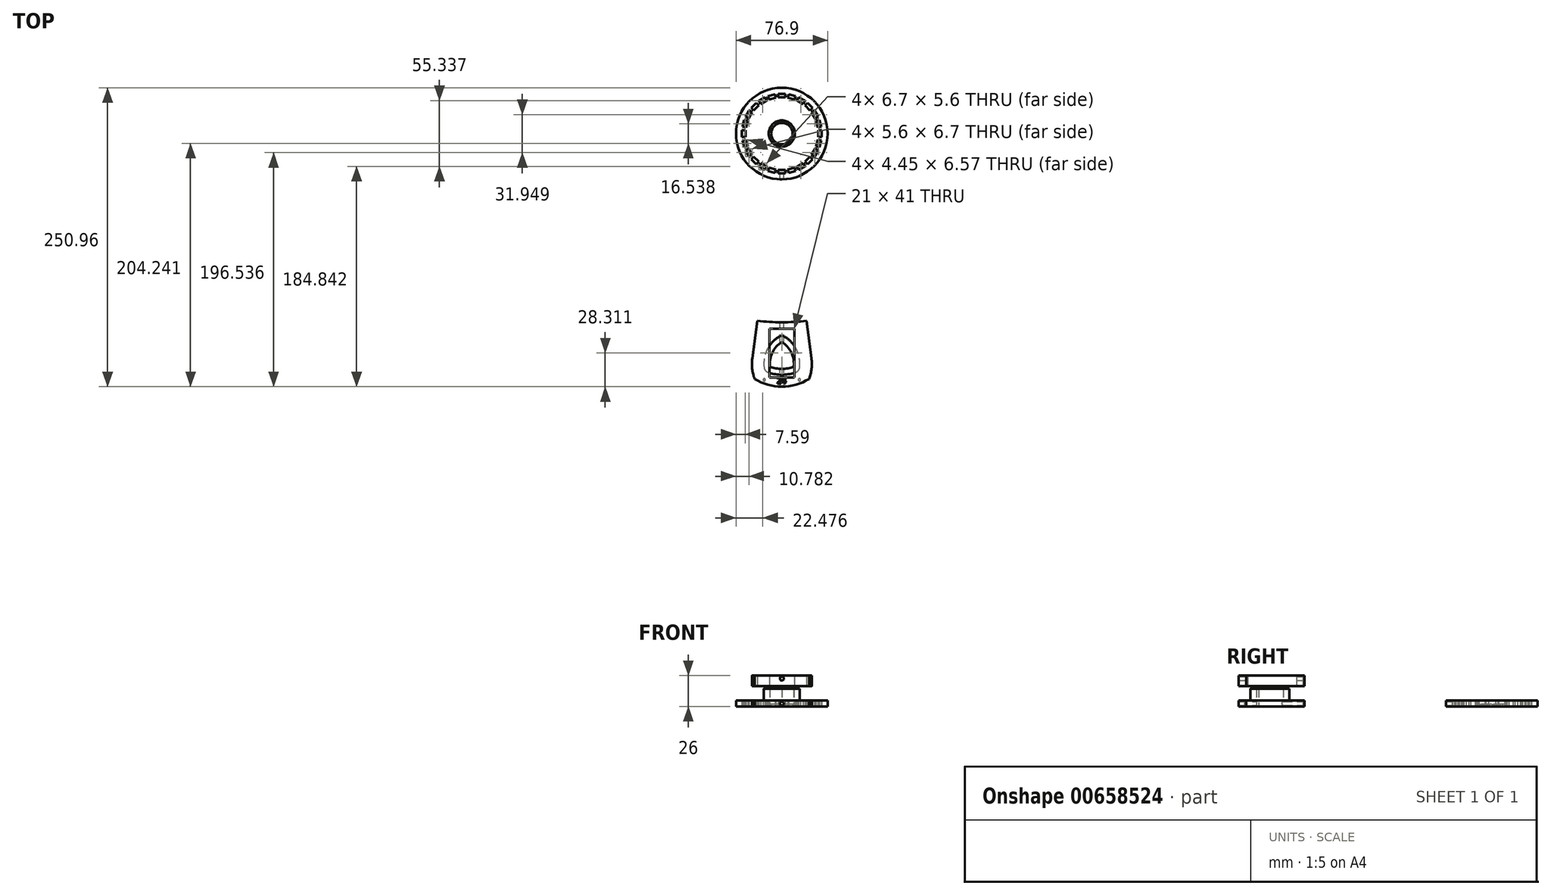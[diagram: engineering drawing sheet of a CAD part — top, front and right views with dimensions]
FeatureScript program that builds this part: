
annotation { "Feature Type Name" : "Feature", "Feature Type Description" : "" }
export const myFeature = defineFeature(function(context is Context, id is Id, definition is map)
    precondition{}
    {
        {
            var Q0;
            Q0=qCreatedBy(makeId("Front.planeOp"),FACE);
            var sketch = newSketch(context, id + "F0", { "sketchPlane" : qUnion([Q0])});
            skLineSegment(sketch, "E0", {"start": v(0, 0) * mm, "end": v(0, 23.65) * mm});
            skSolve(sketch);
        }
        {
            var Q0;
            Q0=qCreatedBy(makeId("Top.planeOp"),FACE);
            var sketch = newSketch(context, id + "F1", { "sketchPlane" : qUnion([Q0])});
            skCircle(sketch, "E1", {"center": v(0, 0) * mm, "radius": 207.24 * mm});
            skArc(sketch, "E2", {"start": v(14.97, -196.23) * mm, "mid": v(12.48, -181.7) * mm, "end": v(2.67, -170.68) * mm});
            skArc(sketch, "E3", {"start": v(-11.77, -200.36) * mm, "mid": v(0, -202.5) * mm, "end": v(11.77, -200.36) * mm});
            skArc(sketch, "E4", {"start": v(-2.67, -170.68) * mm, "mid": v(-12.48, -181.7) * mm, "end": v(-14.97, -196.23) * mm});
            skCircle(sketch, "E5", {"center": v(0, 0) * mm, "radius": 195.94 * mm});
            skArc(sketch, "E6.0", {"start": v(0, -158.43) * mm, "mid": v(-21.5, -177.36) * mm, "end": v(-22.88, -205.97) * mm});
            skArc(sketch, "E6.1", {"start": v(22.88, -205.97) * mm, "mid": v(21.5, -177.36) * mm, "end": v(0, -158.43) * mm});
            skArc(sketch, "E6.2", {"start": v(-22.88, -205.97) * mm, "mid": v(0, -212.5) * mm, "end": v(22.88, -205.97) * mm});
            skCircle(sketch, "E7", {"center": v(0, 0) * mm, "radius": 158.43 * mm});
            skArc(sketch, "E8.filletArc", {"start": v(2.67, -170.68) * mm, "mid": v(0, -169.9) * mm, "end": v(-2.67, -170.68) * mm});
            skPoint(sketch, "E9.visualSharp", {"position": v(-14.47, -199.2) * mm});
            skArc(sketch, "E9.filletArc", {"start": v(-14.97, -196.23) * mm, "mid": v(-13.95, -198.75) * mm, "end": v(-11.77, -200.36) * mm});
            skPoint(sketch, "E10.visualSharp", {"position": v(14.47, -199.2) * mm});
            skArc(sketch, "E10.filletArc", {"start": v(11.77, -200.36) * mm, "mid": v(13.95, -198.75) * mm, "end": v(14.97, -196.23) * mm});
            skLineSegment(sketch, "E11", {"start": v(0, 0) * mm, "end": v(-27.05, -205.47) * mm});
            skLineSegment(sketch, "E12", {"start": v(0, 0) * mm, "end": v(27.05, -205.47) * mm});
            skArc(sketch, "E13.0", {"start": v(0, -174.9) * mm, "mid": v(-7.98, -183.86) * mm, "end": v(-10, -195.68) * mm});
            skArc(sketch, "E13.1", {"start": v(10, -195.68) * mm, "mid": v(7.98, -183.86) * mm, "end": v(0, -174.9) * mm});
            skArc(sketch, "E13.2", {"start": v(-10, -195.68) * mm, "mid": v(0, -197.5) * mm, "end": v(10, -195.68) * mm});
            skPoint(sketch, "E14", {"position": v(-20.68, -157.07) * mm});
            skPoint(sketch, "E15", {"position": v(20.68, -157.07) * mm});
            skCircle(sketch, "E16", {"center": v(-14.75, -206.71) * mm, "radius": 1 * mm});
            skCircle(sketch, "E17", {"center": v(14.75, -206.71) * mm, "radius": 1 * mm});
            skLineSegment(sketch, "E18", {"start": v(-14.47, -199.2) * mm, "end": v(0, -169.2) * mm, "construction": true});
            skLineSegment(sketch, "E19", {"start": v(14.47, -199.2) * mm, "end": v(0, -169.2) * mm, "construction": true});
            skSolve(sketch);
        }
        {
            var Q0;
            {var subQ1=sQuery(id+"F1.wireOp",EDGE,"E6.0");var subQ3=sQuery(id+"F1.wireOp",EDGE,"E11");var subQ4=makeQuery(id+"F1.imprint","INTERSECT",VERTEX,{"derivedFrom":[subQ1,subQ3]});Q0=makeQuery(id+"F1.imprint","IMPRINT",FACE,{"disambiguationData":[TD([[makeQuery(id+"F1.imprint","IMPRINT",EDGE,{"disambiguationData":[TD([[subQ4,1.0]])],"derivedFrom":subQ3}),1.0]])]});}
            var Q1;
            {var subQ1=sQuery(id+"F1.wireOp",EDGE,"E6.1");var subQ3=sQuery(id+"F1.wireOp",EDGE,"E12");var subQ4=makeQuery(id+"F1.imprint","INTERSECT",VERTEX,{"derivedFrom":[subQ1,subQ3]});Q1=makeQuery(id+"F1.imprint","IMPRINT",FACE,{"disambiguationData":[TD([[makeQuery(id+"F1.imprint","IMPRINT",EDGE,{"disambiguationData":[TD([[subQ4,1.0]])],"derivedFrom":subQ3}),-1.0]])]});}
            var Q2;
            {var subQ10=sQuery(id+"F1.wireOp",EDGE,"E2");Q2=makeQuery(id+"F1.imprint","IMPRINT",FACE,{"disambiguationData":[TD([[makeQuery(id+"F1.imprint","IMPRINT",EDGE,{"derivedFrom":subQ10}),-1.0]])]});}
            var Q3;
            {var subQ9=sQuery(id+"F1.wireOp",EDGE,"E3");Q3=makeQuery(id+"F1.imprint","IMPRINT",FACE,{"disambiguationData":[TD([[makeQuery(id+"F1.imprint","IMPRINT",EDGE,{"derivedFrom":subQ9}),-1.0]])]});}
            var Q4;
            {var subQ0=sQuery(id+"F1.wireOp",EDGE,"E6.2");Q4=makeQuery(id+"F1.imprint","IMPRINT",FACE,{"disambiguationData":[TD([[makeQuery(id+"F1.imprint","IMPRINT",EDGE,{"derivedFrom":subQ0}),1.0]])]});}
            extrude(context, id + "F2", {"entities" : qUnion([Q0, Q1, Q2, Q3, Q4]), "depth" : 5 * mm, "offsetDistance" : 25 * mm});
        }
        {
            var Q0;
            {var subQ6=sQuery(id+"F1.wireOp",EDGE,"E2");Q0=makeQuery(id+"F1.imprint","IMPRINT",FACE,{"disambiguationData":[TD([[makeQuery(id+"F1.imprint","IMPRINT",EDGE,{"derivedFrom":subQ6}),1.0]])]});}
            var Q1;
            {var subQ0=sQuery(id+"F1.wireOp",EDGE,"E3");Q1=makeQuery(id+"F1.imprint","IMPRINT",FACE,{"disambiguationData":[TD([[makeQuery(id+"F1.imprint","IMPRINT",EDGE,{"derivedFrom":subQ0}),1.0]])]});}
            extrude(context, id + "F3", {"entities" : qUnion([Q0, Q1]), "operationType" : NewBodyOperationType.ADD, "depth" : 15 * mm, "offsetDistance" : 25 * mm});
        }
        {
            var Q0;
            Q0=makeQuery(id+"F2.opExtrude","SWEPT_EDGE",EDGE,{"disambiguationData":[OSD([sQuery(id+"F1.wireOp",EDGE,"E7"),sQuery(id+"F1.wireOp",EDGE,"E11")])]});
            cPoint(context, id + "F4", {"entities" : qUnion([Q0]), "parameter" : 0.5});
        }
        {
            var Q0;
            Q0=makeQuery(id+"F2.opExtrude","CAP_VERTEX",VERTEX,{"disambiguationData":[OSD([sQuery(id+"F1.wireOp",EDGE,"E7"),sQuery(id+"F1.wireOp",EDGE,"E12")])],"isStart":false});
            var Q1;
            Q1=makeQuery(id+"F2.opExtrude","CAP_VERTEX",VERTEX,{"disambiguationData":[OSD([sQuery(id+"F1.wireOp",EDGE,"E7"),sQuery(id+"F1.wireOp",EDGE,"E11")])],"isStart":false});
            var Q2;
            Q2 = qCreatedBy(id + "F4" ,VERTEX);
            cPlane(context, id + "F5", {"entities" : qUnion([Q0, Q1, Q2]), "cplaneType" : CPlaneType.THREE_POINT, "offset" : 25 * mm, "width" : 150 * mm, "height" : 150 * mm});
        }
        {
            var Q0;
            Q0=makeQuery(id+"F2.opExtrude","CAP_FACE",FACE,{"disambiguationData":[OSD([sQuery(id+"F1.wireOp",EDGE,"E2"),sQuery(id+"F1.wireOp",EDGE,"E3"),sQuery(id+"F1.wireOp",EDGE,"E4"),sQuery(id+"F1.wireOp",EDGE,"E6.0"),sQuery(id+"F1.wireOp",EDGE,"E6.1"),sQuery(id+"F1.wireOp",EDGE,"E6.2"),sQuery(id+"F1.wireOp",EDGE,"E7"),sQuery(id+"F1.wireOp",EDGE,"E8.filletArc"),sQuery(id+"F1.wireOp",EDGE,"E9.filletArc"),sQuery(id+"F1.wireOp",EDGE,"E10.filletArc"),sQuery(id+"F1.wireOp",EDGE,"E11"),sQuery(id+"F1.wireOp",EDGE,"E12"),sQuery(id+"F1.wireOp",EDGE,"E16"),sQuery(id+"F1.wireOp",EDGE,"E17")])],"isStart":false});
            var sketch = newSketch(context, id + "F6", { "sketchPlane" : qUnion([Q0])});
            skText(sketch, "E20", { "text": "24\n", "fontName": "OpenSans-Regular.ttf"});
            skPoint(sketch, "E21", {"position": v(0, -207.24) * mm});
            const initialGuessF6  = {"E20": [-0.00413, -0.20974, 1, 0, 0.005]};
            skSetInitialGuess(sketch, initialGuessF6);
            skSolve(sketch);
        }
        {
            var Q0;
            Q0 = qSketchRegion(id + "F6", true);
            extrude(context, id + "F7", {"entities" : qUnion([Q0]), "operationType" : NewBodyOperationType.REMOVE, "depth" : -0.4 * mm, "offsetDistance" : 25 * mm});
        }
        {
            var Q0;
            Q0=qCreatedBy(id+"F5.planeOp",FACE);
            var sketch = newSketch(context, id + "F8", { "sketchPlane" : qUnion([Q0])});
            skPoint(sketch, "E22.0", {"position": v(-20.68, 5) * mm});
            skPoint(sketch, "E23.0", {"position": v(20.68, 5) * mm});
            skPoint(sketch, "E24", {"position": v(0, 2.5) * mm});
            skPoint(sketch, "E25.0", {"position": v(20.68, 0) * mm});
            skPoint(sketch, "E26.0", {"position": v(-20.68, 0) * mm});
            skSolve(sketch);
        }
        {
            var Q0;
            Q0=sQuery(id+"F8.wireOp",VERTEX,"E24");
            var Q1;
            Q1=makeQuery(id+"F2.opExtrude","SWEPT_BODY",BODY,{"disambiguationData":[OSD([sQuery(id+"F1.wireOp",EDGE,"E2"),sQuery(id+"F1.wireOp",EDGE,"E3"),sQuery(id+"F1.wireOp",EDGE,"E4"),sQuery(id+"F1.wireOp",EDGE,"E6.0"),sQuery(id+"F1.wireOp",EDGE,"E6.1"),sQuery(id+"F1.wireOp",EDGE,"E6.2"),sQuery(id+"F1.wireOp",EDGE,"E7"),sQuery(id+"F1.wireOp",EDGE,"E8.filletArc"),sQuery(id+"F1.wireOp",EDGE,"E9.filletArc"),sQuery(id+"F1.wireOp",EDGE,"E10.filletArc"),sQuery(id+"F1.wireOp",EDGE,"E11"),sQuery(id+"F1.wireOp",EDGE,"E12")])]});
            hole(context, id + "F9", {"style" : HoleStyle.SIMPLE, "endStyle" : HoleEndStyle.THROUGH, "standardTappedOrClearance" : lookupTablePath({ "fit" : "Normal", "standard" : "ISO", "size" : "M3", "type" : "Clearance" }), "standardBlindInLast" : lookupTablePath({ "fit" : "Standard", "standard" : "ISO", "size" : "M3", "type" : "Clearance" }), "holeDiameter" : 3.3 * mm, "majorDiameter" : 5 * mm, "isTappedThrough" : true, "tappedDepth" : 12 * mm, "tapClearance" : 3, "startFromSketch" : true, "locations" : qUnion([Q0]), "scope" : qUnion([Q1])});
        }
        {
            var Q0;
            Q0=qCreatedBy(makeId("Top.planeOp"),FACE);
            var sketch = newSketch(context, id + "F10", { "sketchPlane" : qUnion([Q0])});
            skCircle(sketch, "E27", {"center": v(0, 0) * mm, "radius": 38.45 * mm});
            skLineSegment(sketch, "E28.bottom", {"start": v(-3, -30.45) * mm, "end": v(3, -30.45) * mm});
            skLineSegment(sketch, "E28.top", {"start": v(-3, -33.45) * mm, "end": v(3, -33.45) * mm});
            skLineSegment(sketch, "E28.left", {"start": v(-3, -30.45) * mm, "end": v(-3, -33.45) * mm});
            skLineSegment(sketch, "E28.right", {"start": v(3, -30.45) * mm, "end": v(3, -33.45) * mm});
            skCircle(sketch, "E29", {"center": v(0, 0) * mm, "radius": 11 * mm});
            skLineSegment(sketch, "E30.1.0", {"start": v(-10.78, -28.63) * mm, "end": v(-4.98, -30.19) * mm});
            skLineSegment(sketch, "E30.1.1", {"start": v(-4.98, -30.19) * mm, "end": v(-5.76, -33.09) * mm});
            skLineSegment(sketch, "E30.1.2", {"start": v(-11.55, -31.53) * mm, "end": v(-5.76, -33.09) * mm});
            skLineSegment(sketch, "E30.1.3", {"start": v(-10.78, -28.63) * mm, "end": v(-11.55, -31.53) * mm});
            skLineSegment(sketch, "E30.2.0", {"start": v(-17.82, -24.87) * mm, "end": v(-12.63, -27.87) * mm});
            skLineSegment(sketch, "E30.2.1", {"start": v(-12.63, -27.87) * mm, "end": v(-14.13, -30.47) * mm});
            skLineSegment(sketch, "E30.2.2", {"start": v(-19.32, -27.47) * mm, "end": v(-14.13, -30.47) * mm});
            skLineSegment(sketch, "E30.2.3", {"start": v(-17.82, -24.87) * mm, "end": v(-19.32, -27.47) * mm});
            skLineSegment(sketch, "E30.3.0", {"start": v(-23.65, -19.4) * mm, "end": v(-19.4, -23.65) * mm});
            skLineSegment(sketch, "E30.3.1", {"start": v(-19.4, -23.65) * mm, "end": v(-21.53, -25.77) * mm});
            skLineSegment(sketch, "E30.3.2", {"start": v(-25.77, -21.53) * mm, "end": v(-21.53, -25.77) * mm});
            skLineSegment(sketch, "E30.3.3", {"start": v(-23.65, -19.4) * mm, "end": v(-25.77, -21.53) * mm});
            skLineSegment(sketch, "E30.4.0", {"start": v(-27.87, -12.63) * mm, "end": v(-24.87, -17.82) * mm});
            skLineSegment(sketch, "E30.4.1", {"start": v(-24.87, -17.82) * mm, "end": v(-27.47, -19.32) * mm});
            skLineSegment(sketch, "E30.4.2", {"start": v(-30.47, -14.13) * mm, "end": v(-27.47, -19.32) * mm});
            skLineSegment(sketch, "E30.4.3", {"start": v(-27.87, -12.63) * mm, "end": v(-30.47, -14.13) * mm});
            skLineSegment(sketch, "E30.5.0", {"start": v(-30.19, -4.98) * mm, "end": v(-28.63, -10.78) * mm});
            skLineSegment(sketch, "E30.5.1", {"start": v(-28.63, -10.78) * mm, "end": v(-31.53, -11.55) * mm});
            skLineSegment(sketch, "E30.5.2", {"start": v(-33.09, -5.76) * mm, "end": v(-31.53, -11.55) * mm});
            skLineSegment(sketch, "E30.5.3", {"start": v(-30.19, -4.98) * mm, "end": v(-33.09, -5.76) * mm});
            skLineSegment(sketch, "E30.6.0", {"start": v(-30.45, 3) * mm, "end": v(-30.45, -3) * mm});
            skLineSegment(sketch, "E30.6.1", {"start": v(-30.45, -3) * mm, "end": v(-33.45, -3) * mm});
            skLineSegment(sketch, "E30.6.2", {"start": v(-33.45, 3) * mm, "end": v(-33.45, -3) * mm});
            skLineSegment(sketch, "E30.6.3", {"start": v(-30.45, 3) * mm, "end": v(-33.45, 3) * mm});
            skLineSegment(sketch, "E30.7.0", {"start": v(-28.63, 10.78) * mm, "end": v(-30.19, 4.98) * mm});
            skLineSegment(sketch, "E30.7.1", {"start": v(-30.19, 4.98) * mm, "end": v(-33.09, 5.76) * mm});
            skLineSegment(sketch, "E30.7.2", {"start": v(-31.53, 11.55) * mm, "end": v(-33.09, 5.76) * mm});
            skLineSegment(sketch, "E30.7.3", {"start": v(-28.63, 10.78) * mm, "end": v(-31.53, 11.55) * mm});
            skLineSegment(sketch, "E30.8.0", {"start": v(-24.87, 17.82) * mm, "end": v(-27.87, 12.63) * mm});
            skLineSegment(sketch, "E30.8.1", {"start": v(-27.87, 12.63) * mm, "end": v(-30.47, 14.13) * mm});
            skLineSegment(sketch, "E30.8.2", {"start": v(-27.47, 19.32) * mm, "end": v(-30.47, 14.13) * mm});
            skLineSegment(sketch, "E30.8.3", {"start": v(-24.87, 17.82) * mm, "end": v(-27.47, 19.32) * mm});
            skLineSegment(sketch, "E30.9.0", {"start": v(-19.4, 23.65) * mm, "end": v(-23.65, 19.4) * mm});
            skLineSegment(sketch, "E30.9.1", {"start": v(-23.65, 19.4) * mm, "end": v(-25.77, 21.53) * mm});
            skLineSegment(sketch, "E30.9.2", {"start": v(-21.53, 25.77) * mm, "end": v(-25.77, 21.53) * mm});
            skLineSegment(sketch, "E30.9.3", {"start": v(-19.4, 23.65) * mm, "end": v(-21.53, 25.77) * mm});
            skLineSegment(sketch, "E30.10.0", {"start": v(-12.63, 27.87) * mm, "end": v(-17.82, 24.87) * mm});
            skLineSegment(sketch, "E30.10.1", {"start": v(-17.82, 24.87) * mm, "end": v(-19.32, 27.47) * mm});
            skLineSegment(sketch, "E30.10.2", {"start": v(-14.13, 30.47) * mm, "end": v(-19.32, 27.47) * mm});
            skLineSegment(sketch, "E30.10.3", {"start": v(-12.63, 27.87) * mm, "end": v(-14.13, 30.47) * mm});
            skLineSegment(sketch, "E30.11.0", {"start": v(-4.98, 30.19) * mm, "end": v(-10.78, 28.63) * mm});
            skLineSegment(sketch, "E30.11.1", {"start": v(-10.78, 28.63) * mm, "end": v(-11.55, 31.53) * mm});
            skLineSegment(sketch, "E30.11.2", {"start": v(-5.76, 33.09) * mm, "end": v(-11.55, 31.53) * mm});
            skLineSegment(sketch, "E30.11.3", {"start": v(-4.98, 30.19) * mm, "end": v(-5.76, 33.09) * mm});
            skLineSegment(sketch, "E30.anchor1", {"start": v(0, 0) * mm, "end": v(-3, -30.45) * mm, "construction": true});
            skLineSegment(sketch, "E30.anchor2", {"start": v(0, 0) * mm, "end": v(4.98, -30.19) * mm, "construction": true});
            skCircle(sketch, "E31", {"center": v(0, 0) * mm, "radius": 9 * mm});
            skLineSegment(sketch, "E32.1.12.0", {"start": v(3, 30.45) * mm, "end": v(-3, 30.45) * mm});
            skLineSegment(sketch, "E32.3.12.0", {"start": v(-3, 30.45) * mm, "end": v(-3, 33.45) * mm});
            skLineSegment(sketch, "E32.6.12.0", {"start": v(3, 33.45) * mm, "end": v(-3, 33.45) * mm});
            skLineSegment(sketch, "E32.9.12.0", {"start": v(3, 30.45) * mm, "end": v(3, 33.45) * mm});
            skLineSegment(sketch, "E32.1.13.0", {"start": v(10.78, 28.63) * mm, "end": v(4.98, 30.19) * mm});
            skLineSegment(sketch, "E32.3.13.0", {"start": v(4.98, 30.19) * mm, "end": v(5.76, 33.09) * mm});
            skLineSegment(sketch, "E32.6.13.0", {"start": v(11.55, 31.53) * mm, "end": v(5.76, 33.09) * mm});
            skLineSegment(sketch, "E32.9.13.0", {"start": v(10.78, 28.63) * mm, "end": v(11.55, 31.53) * mm});
            skLineSegment(sketch, "E32.1.14.0", {"start": v(17.82, 24.87) * mm, "end": v(12.63, 27.87) * mm});
            skLineSegment(sketch, "E32.3.14.0", {"start": v(12.63, 27.87) * mm, "end": v(14.13, 30.47) * mm});
            skLineSegment(sketch, "E32.6.14.0", {"start": v(19.32, 27.47) * mm, "end": v(14.13, 30.47) * mm});
            skLineSegment(sketch, "E32.9.14.0", {"start": v(17.82, 24.87) * mm, "end": v(19.32, 27.47) * mm});
            skLineSegment(sketch, "E32.1.15.0", {"start": v(23.65, 19.4) * mm, "end": v(19.4, 23.65) * mm});
            skLineSegment(sketch, "E32.3.15.0", {"start": v(19.4, 23.65) * mm, "end": v(21.53, 25.77) * mm});
            skLineSegment(sketch, "E32.6.15.0", {"start": v(25.77, 21.53) * mm, "end": v(21.53, 25.77) * mm});
            skLineSegment(sketch, "E32.9.15.0", {"start": v(23.65, 19.4) * mm, "end": v(25.77, 21.53) * mm});
            skLineSegment(sketch, "E32.1.16.0", {"start": v(27.87, 12.63) * mm, "end": v(24.87, 17.82) * mm});
            skLineSegment(sketch, "E32.3.16.0", {"start": v(24.87, 17.82) * mm, "end": v(27.47, 19.32) * mm});
            skLineSegment(sketch, "E32.6.16.0", {"start": v(30.47, 14.13) * mm, "end": v(27.47, 19.32) * mm});
            skLineSegment(sketch, "E32.9.16.0", {"start": v(27.87, 12.63) * mm, "end": v(30.47, 14.13) * mm});
            skLineSegment(sketch, "E32.1.17.0", {"start": v(30.19, 4.98) * mm, "end": v(28.63, 10.78) * mm});
            skLineSegment(sketch, "E32.3.17.0", {"start": v(28.63, 10.78) * mm, "end": v(31.53, 11.55) * mm});
            skLineSegment(sketch, "E32.6.17.0", {"start": v(33.09, 5.76) * mm, "end": v(31.53, 11.55) * mm});
            skLineSegment(sketch, "E32.9.17.0", {"start": v(30.19, 4.98) * mm, "end": v(33.09, 5.76) * mm});
            skLineSegment(sketch, "E32.1.18.0", {"start": v(30.45, -3) * mm, "end": v(30.45, 3) * mm});
            skLineSegment(sketch, "E32.3.18.0", {"start": v(30.45, 3) * mm, "end": v(33.45, 3) * mm});
            skLineSegment(sketch, "E32.6.18.0", {"start": v(33.45, -3) * mm, "end": v(33.45, 3) * mm});
            skLineSegment(sketch, "E32.9.18.0", {"start": v(30.45, -3) * mm, "end": v(33.45, -3) * mm});
            skLineSegment(sketch, "E32.1.19.0", {"start": v(28.63, -10.78) * mm, "end": v(30.19, -4.98) * mm});
            skLineSegment(sketch, "E32.3.19.0", {"start": v(30.19, -4.98) * mm, "end": v(33.09, -5.76) * mm});
            skLineSegment(sketch, "E32.6.19.0", {"start": v(31.53, -11.55) * mm, "end": v(33.09, -5.76) * mm});
            skLineSegment(sketch, "E32.9.19.0", {"start": v(28.63, -10.78) * mm, "end": v(31.53, -11.55) * mm});
            skLineSegment(sketch, "E32.1.20.0", {"start": v(24.87, -17.82) * mm, "end": v(27.87, -12.63) * mm});
            skLineSegment(sketch, "E32.3.20.0", {"start": v(27.87, -12.63) * mm, "end": v(30.47, -14.13) * mm});
            skLineSegment(sketch, "E32.6.20.0", {"start": v(27.47, -19.32) * mm, "end": v(30.47, -14.13) * mm});
            skLineSegment(sketch, "E32.9.20.0", {"start": v(24.87, -17.82) * mm, "end": v(27.47, -19.32) * mm});
            skLineSegment(sketch, "E32.1.21.0", {"start": v(19.4, -23.65) * mm, "end": v(23.65, -19.4) * mm});
            skLineSegment(sketch, "E32.3.21.0", {"start": v(23.65, -19.4) * mm, "end": v(25.77, -21.53) * mm});
            skLineSegment(sketch, "E32.6.21.0", {"start": v(21.53, -25.77) * mm, "end": v(25.77, -21.53) * mm});
            skLineSegment(sketch, "E32.9.21.0", {"start": v(19.4, -23.65) * mm, "end": v(21.53, -25.77) * mm});
            skLineSegment(sketch, "E32.1.22.0", {"start": v(12.63, -27.87) * mm, "end": v(17.82, -24.87) * mm});
            skLineSegment(sketch, "E32.3.22.0", {"start": v(17.82, -24.87) * mm, "end": v(19.32, -27.47) * mm});
            skLineSegment(sketch, "E32.6.22.0", {"start": v(14.13, -30.47) * mm, "end": v(19.32, -27.47) * mm});
            skLineSegment(sketch, "E32.9.22.0", {"start": v(12.63, -27.87) * mm, "end": v(14.13, -30.47) * mm});
            skLineSegment(sketch, "E32.1.23.0", {"start": v(4.98, -30.19) * mm, "end": v(10.78, -28.63) * mm});
            skLineSegment(sketch, "E32.3.23.0", {"start": v(10.78, -28.63) * mm, "end": v(11.55, -31.53) * mm});
            skLineSegment(sketch, "E32.6.23.0", {"start": v(5.76, -33.09) * mm, "end": v(11.55, -31.53) * mm});
            skLineSegment(sketch, "E32.9.23.0", {"start": v(4.98, -30.19) * mm, "end": v(5.76, -33.09) * mm});
            skSolve(sketch);
        }
        {
            var Q0;
            Q0=makeQuery(id+"F10.imprint","IMPRINT",FACE,{"disambiguationData":[TD([[makeQuery(id+"F10.imprint","IMPRINT",EDGE,{"derivedFrom":sQuery(id+"F10.wireOp",EDGE,"E27")}),1.0]])]});
            extrude(context, id + "F11", {"entities" : qUnion([Q0]), "depth" : 5 * mm, "offsetDistance" : 25 * mm});
        }
        {
            var Q0;
            Q0=makeQuery(id+"F10.imprint","IMPRINT",FACE,{"disambiguationData":[TD([[makeQuery(id+"F10.imprint","IMPRINT",EDGE,{"derivedFrom":sQuery(id+"F10.wireOp",EDGE,"E29")}),1.0]])]});
            extrude(context, id + "F12", {"entities" : qUnion([Q0]), "operationType" : NewBodyOperationType.ADD, "depth" : 2 * mm, "offsetDistance" : 25 * mm});
        }
        {
            var Q0;
            Q0=makeQuery(id+"F11.opExtrude","SWEPT_FACE",FACE,{"disambiguationData":[OSD([sQuery(id+"F10.wireOp",EDGE,"E28.top")])]});
            var sketch = newSketch(context, id + "F13", { "sketchPlane" : qUnion([Q0])});
            skLineSegment(sketch, "E33.0.0", {"start": v(-3, 0) * mm, "end": v(3, 0) * mm});
            skLineSegment(sketch, "E33.0.1", {"start": v(3, 0) * mm, "end": v(3, 5) * mm});
            skLineSegment(sketch, "E33.0.2", {"start": v(3, 5) * mm, "end": v(-3, 5) * mm});
            skLineSegment(sketch, "E33.0.3", {"start": v(-3, 5) * mm, "end": v(-3, 0) * mm});
            skPoint(sketch, "E34.0", {"position": v(0, 2.5) * mm});
            skSolve(sketch);
        }
        {
            var Q0;
            Q0=sQuery(id+"F13.wireOp",VERTEX,"E34.0");
            var Q1;
            Q1=makeQuery(id+"F11.opExtrude","SWEPT_BODY",BODY,{"disambiguationData":[OSD([sQuery(id+"F10.wireOp",EDGE,"E27"),sQuery(id+"F10.wireOp",EDGE,"E28.bottom"),sQuery(id+"F10.wireOp",EDGE,"E28.top"),sQuery(id+"F10.wireOp",EDGE,"E28.left"),sQuery(id+"F10.wireOp",EDGE,"E28.right"),sQuery(id+"F10.wireOp",EDGE,"E29"),sQuery(id+"F10.wireOp",EDGE,"E30.1.0"),sQuery(id+"F10.wireOp",EDGE,"E30.1.1"),sQuery(id+"F10.wireOp",EDGE,"E30.1.2"),sQuery(id+"F10.wireOp",EDGE,"E30.1.3"),sQuery(id+"F10.wireOp",EDGE,"E30.2.0"),sQuery(id+"F10.wireOp",EDGE,"E30.2.1"),sQuery(id+"F10.wireOp",EDGE,"E30.2.2"),sQuery(id+"F10.wireOp",EDGE,"E30.2.3"),sQuery(id+"F10.wireOp",EDGE,"E30.3.0"),sQuery(id+"F10.wireOp",EDGE,"E30.3.1"),sQuery(id+"F10.wireOp",EDGE,"E30.3.2"),sQuery(id+"F10.wireOp",EDGE,"E30.3.3"),sQuery(id+"F10.wireOp",EDGE,"E30.4.0"),sQuery(id+"F10.wireOp",EDGE,"E30.4.1"),sQuery(id+"F10.wireOp",EDGE,"E30.4.2"),sQuery(id+"F10.wireOp",EDGE,"E30.4.3"),sQuery(id+"F10.wireOp",EDGE,"E30.5.0"),sQuery(id+"F10.wireOp",EDGE,"E30.5.1"),sQuery(id+"F10.wireOp",EDGE,"E30.5.2"),sQuery(id+"F10.wireOp",EDGE,"E30.5.3"),sQuery(id+"F10.wireOp",EDGE,"E30.6.0"),sQuery(id+"F10.wireOp",EDGE,"E30.6.1"),sQuery(id+"F10.wireOp",EDGE,"E30.6.2"),sQuery(id+"F10.wireOp",EDGE,"E30.6.3"),sQuery(id+"F10.wireOp",EDGE,"E30.7.0"),sQuery(id+"F10.wireOp",EDGE,"E30.7.1"),sQuery(id+"F10.wireOp",EDGE,"E30.7.2"),sQuery(id+"F10.wireOp",EDGE,"E30.7.3"),sQuery(id+"F10.wireOp",EDGE,"E30.8.0"),sQuery(id+"F10.wireOp",EDGE,"E30.8.1"),sQuery(id+"F10.wireOp",EDGE,"E30.8.2"),sQuery(id+"F10.wireOp",EDGE,"E30.8.3"),sQuery(id+"F10.wireOp",EDGE,"E30.9.0"),sQuery(id+"F10.wireOp",EDGE,"E30.9.1"),sQuery(id+"F10.wireOp",EDGE,"E30.9.2"),sQuery(id+"F10.wireOp",EDGE,"E30.9.3"),sQuery(id+"F10.wireOp",EDGE,"E30.10.0"),sQuery(id+"F10.wireOp",EDGE,"E30.10.1"),sQuery(id+"F10.wireOp",EDGE,"E30.10.2"),sQuery(id+"F10.wireOp",EDGE,"E30.10.3"),sQuery(id+"F10.wireOp",EDGE,"E30.11.0"),sQuery(id+"F10.wireOp",EDGE,"E30.11.1"),sQuery(id+"F10.wireOp",EDGE,"E30.11.2"),sQuery(id+"F10.wireOp",EDGE,"E30.11.3"),sQuery(id+"F10.wireOp",EDGE,"E30.12.0"),sQuery(id+"F10.wireOp",EDGE,"E30.12.1"),sQuery(id+"F10.wireOp",EDGE,"E30.12.2"),sQuery(id+"F10.wireOp",EDGE,"E30.12.3"),sQuery(id+"F10.wireOp",EDGE,"E30.13.0"),sQuery(id+"F10.wireOp",EDGE,"E30.13.1"),sQuery(id+"F10.wireOp",EDGE,"E30.13.2"),sQuery(id+"F10.wireOp",EDGE,"E30.13.3"),sQuery(id+"F10.wireOp",EDGE,"E30.14.0"),sQuery(id+"F10.wireOp",EDGE,"E30.14.1"),sQuery(id+"F10.wireOp",EDGE,"E30.14.2"),sQuery(id+"F10.wireOp",EDGE,"E30.14.3")])]});
            hole(context, id + "F14", {"style" : HoleStyle.SIMPLE, "endStyle" : HoleEndStyle.THROUGH, "standardTappedOrClearance" : lookupTablePath({ "fit" : "Normal", "standard" : "ISO", "size" : "M3", "type" : "Clearance" }), "standardBlindInLast" : lookupTablePath({ "fit" : "Standard", "standard" : "ISO", "size" : "M3", "type" : "Clearance" }), "holeDiameter" : 3.3 * mm, "majorDiameter" : 5 * mm, "isTappedThrough" : true, "tappedDepth" : 12 * mm, "tapClearance" : 3, "startFromSketch" : true, "locations" : qUnion([Q0]), "scope" : qUnion([Q1])});
        }
        {
            var Q0;
            Q0=makeQuery(id+"F3.opExtrude","CAP_FACE",FACE,{"disambiguationData":[OSD([sQuery(id+"F1.wireOp",EDGE,"E2"),sQuery(id+"F1.wireOp",EDGE,"E3"),sQuery(id+"F1.wireOp",EDGE,"E4"),sQuery(id+"F1.wireOp",EDGE,"E8.filletArc"),sQuery(id+"F1.wireOp",EDGE,"E9.filletArc"),sQuery(id+"F1.wireOp",EDGE,"E10.filletArc"),sQuery(id+"F1.wireOp",EDGE,"E13.0"),sQuery(id+"F1.wireOp",EDGE,"E13.1"),sQuery(id+"F1.wireOp",EDGE,"E13.2")])],"isStart":false});
            cPlane(context, id + "F15", {"entities" : qUnion([Q0]), "cplaneType" : CPlaneType.OFFSET, "offset" : 2 * mm, "width" : 150 * mm, "height" : 150 * mm});
        }
        {
            var Q0;
            Q0=qCreatedBy(id+"F15.planeOp",FACE);
            var sketch = newSketch(context, id + "F16", { "sketchPlane" : qUnion([Q0])});
            skLineSegment(sketch, "E35.bottom", {"start": v(-10, -164.2) * mm, "end": v(10, -164.2) * mm, "construction": true});
            skLineSegment(sketch, "E35.top", {"start": v(-10, -204.2) * mm, "end": v(10, -204.2) * mm, "construction": true});
            skLineSegment(sketch, "E35.left", {"start": v(-10, -164.2) * mm, "end": v(-10, -204.2) * mm, "construction": true});
            skLineSegment(sketch, "E35.right", {"start": v(10, -164.2) * mm, "end": v(10, -204.2) * mm, "construction": true});
            skLineSegment(sketch, "E36.0", {"start": v(0, 0) * mm, "end": v(-27.05, -205.47) * mm});
            skCircle(sketch, "E37.0", {"center": v(0, 0) * mm, "radius": 158.43 * mm});
            skLineSegment(sketch, "E38.0", {"start": v(0, 0) * mm, "end": v(27.05, -205.47) * mm});
            skArc(sketch, "E39.0", {"start": v(0, -158.43) * mm, "mid": v(-21.5, -177.36) * mm, "end": v(-22.88, -205.97) * mm});
            skArc(sketch, "E40.0", {"start": v(22.88, -205.97) * mm, "mid": v(21.5, -177.36) * mm, "end": v(0, -158.43) * mm});
            skArc(sketch, "E41.0", {"start": v(-22.88, -205.97) * mm, "mid": v(0, -212.5) * mm, "end": v(22.88, -205.97) * mm});
            skLineSegment(sketch, "E42", {"start": v(0, -169.2) * mm, "end": v(0, -176.7) * mm, "construction": true});
            skLineSegment(sketch, "E43", {"start": v(0, -176.7) * mm, "end": v(0, -184.2) * mm, "construction": true});
            skPoint(sketch, "E44.0", {"position": v(-14.47, -199.2) * mm});
            skPoint(sketch, "E45.0", {"position": v(14.47, -199.2) * mm});
            skLineSegment(sketch, "E46", {"start": v(-14.47, -199.2) * mm, "end": v(0, -199.2) * mm, "construction": true});
            skLineSegment(sketch, "E47", {"start": v(0, -199.2) * mm, "end": v(14.47, -199.2) * mm, "construction": true});
            skLineSegment(sketch, "E48", {"start": v(0, -184.2) * mm, "end": v(0, -191.7) * mm, "construction": true});
            skLineSegment(sketch, "E49", {"start": v(0, -191.7) * mm, "end": v(0, -199.2) * mm, "construction": true});
            skLineSegment(sketch, "E50.0", {"start": v(-10.5, -163.7) * mm, "end": v(10.5, -163.7) * mm});
            skLineSegment(sketch, "E50.1", {"start": v(-10.5, -163.7) * mm, "end": v(-10.5, -204.7) * mm});
            skLineSegment(sketch, "E50.2", {"start": v(-10.5, -204.7) * mm, "end": v(10.5, -204.7) * mm});
            skLineSegment(sketch, "E50.3", {"start": v(10.5, -163.7) * mm, "end": v(10.5, -204.7) * mm});
            skSolve(sketch);
        }
        {
            var Q0;
            {var subQ0=sQuery(id+"F16.wireOp",EDGE,"E39.0");var subQ1=sQuery(id+"F16.wireOp",EDGE,"E36.0");var subQ2=makeQuery(id+"F16.imprint","INTERSECT",VERTEX,{"derivedFrom":[subQ1,subQ0]});Q0=makeQuery(id+"F16.imprint","IMPRINT",FACE,{"disambiguationData":[TD([[makeQuery(id+"F16.imprint","IMPRINT",EDGE,{"disambiguationData":[TD([[subQ2,1.0]])],"derivedFrom":subQ1}),1.0]])]});}
            var Q1;
            {var subQ0=sQuery(id+"F16.wireOp",EDGE,"E40.0");var subQ5=sQuery(id+"F16.wireOp",EDGE,"E38.0");var subQ7=makeQuery(id+"F16.imprint","INTERSECT",VERTEX,{"derivedFrom":[subQ5,subQ0]});Q1=makeQuery(id+"F16.imprint","IMPRINT",FACE,{"disambiguationData":[TD([[makeQuery(id+"F16.imprint","IMPRINT",EDGE,{"disambiguationData":[TD([[subQ7,1.0]])],"derivedFrom":subQ5}),-1.0]])]});}
            var Q2;
            {var subQ5=sQuery(id+"F16.wireOp",EDGE,"E41.0");Q2=makeQuery(id+"F16.imprint","IMPRINT",FACE,{"disambiguationData":[TD([[makeQuery(id+"F16.imprint","IMPRINT",EDGE,{"derivedFrom":subQ5}),1.0]])]});}
            var Q3;
            {var subQ1=sQuery(id+"F16.wireOp",EDGE,"E39.0");var subQ3=sQuery(id+"F16.wireOp",EDGE,"E50.0");var subQ4=makeQuery(id+"F16.imprint","INTERSECT",VERTEX,{"derivedFrom":[subQ1,subQ3]});Q3=makeQuery(id+"F16.imprint","IMPRINT",FACE,{"disambiguationData":[TD([[makeQuery(id+"F16.imprint","IMPRINT",EDGE,{"disambiguationData":[TD([[subQ4,-1.0]])],"derivedFrom":subQ3}),1.0]])]});}
            extrude(context, id + "F17", {"entities" : qUnion([Q0, Q1, Q2, Q3]), "depth" : 9 * mm, "offsetDistance" : 25 * mm});
        }
        {
            var Q0;
            Q0=makeQuery(id+"F17.opExtrude","CAP_VERTEX",VERTEX,{"disambiguationData":[OSD([sQuery(id+"F16.wireOp",EDGE,"E37.0"),sQuery(id+"F16.wireOp",EDGE,"E38.0")])],"isStart":false});
            var Q1;
            Q1=makeQuery(id+"F17.opExtrude","CAP_VERTEX",VERTEX,{"disambiguationData":[OSD([sQuery(id+"F16.wireOp",EDGE,"E36.0"),sQuery(id+"F16.wireOp",EDGE,"E37.0")])],"isStart":true});
            var Q2;
            Q2=makeQuery(id+"F17.opExtrude","CAP_VERTEX",VERTEX,{"disambiguationData":[OSD([sQuery(id+"F16.wireOp",EDGE,"E36.0"),sQuery(id+"F16.wireOp",EDGE,"E37.0")])],"isStart":false});
            cPlane(context, id + "F18", {"entities" : qUnion([Q0, Q1, Q2]), "cplaneType" : CPlaneType.THREE_POINT, "offset" : 25 * mm, "width" : 150 * mm, "height" : 150 * mm});
        }
        {
            var Q0;
            Q0=qCreatedBy(id+"F18.planeOp",FACE);
            var sketch = newSketch(context, id + "F19", { "sketchPlane" : qUnion([Q0])});
            skPoint(sketch, "E51", {"position": v(0, 23.5) * mm});
            skSolve(sketch);
        }
        {
            var Q0;
            Q0=sQuery(id+"F19.wireOp",VERTEX,"E51");
            var Q1;
            Q1=makeQuery(id+"F17.opExtrude","SWEPT_BODY",BODY,{"disambiguationData":[OSD([sQuery(id+"F16.wireOp",EDGE,"E36.0"),sQuery(id+"F16.wireOp",EDGE,"E37.0"),sQuery(id+"F16.wireOp",EDGE,"E38.0"),sQuery(id+"F16.wireOp",EDGE,"E39.0"),sQuery(id+"F16.wireOp",EDGE,"E40.0"),sQuery(id+"F16.wireOp",EDGE,"E41.0"),sQuery(id+"F16.wireOp",EDGE,"E50.0"),sQuery(id+"F16.wireOp",EDGE,"E50.1"),sQuery(id+"F16.wireOp",EDGE,"E50.2"),sQuery(id+"F16.wireOp",EDGE,"E50.3")])]});
            hole(context, id + "F20", {"style" : HoleStyle.SIMPLE, "endStyle" : HoleEndStyle.THROUGH, "oppositeDirection" : true, "standardTappedOrClearance" : lookupTablePath({ "fit" : "Normal", "standard" : "ISO", "size" : "M3", "type" : "Clearance" }), "standardBlindInLast" : lookupTablePath({ "fit" : "Standard", "standard" : "ISO", "size" : "M3", "type" : "Clearance" }), "holeDiameter" : 3.3 * mm, "majorDiameter" : 5 * mm, "isTappedThrough" : true, "tappedDepth" : 12 * mm, "tapClearance" : 3, "startFromSketch" : true, "locations" : qUnion([Q0]), "scope" : qUnion([Q1])});
        }
        {
            var Q0;
            Q0=makeQuery(id+"F17.opExtrude","CAP_FACE",FACE,{"disambiguationData":[OSD([sQuery(id+"F16.wireOp",EDGE,"E36.0"),sQuery(id+"F16.wireOp",EDGE,"E37.0"),sQuery(id+"F16.wireOp",EDGE,"E38.0"),sQuery(id+"F16.wireOp",EDGE,"E39.0"),sQuery(id+"F16.wireOp",EDGE,"E40.0"),sQuery(id+"F16.wireOp",EDGE,"E41.0"),sQuery(id+"F16.wireOp",EDGE,"E50.0"),sQuery(id+"F16.wireOp",EDGE,"E50.1"),sQuery(id+"F16.wireOp",EDGE,"E50.2"),sQuery(id+"F16.wireOp",EDGE,"E50.3")])],"isStart":false});
            var sketch = newSketch(context, id + "F21", { "sketchPlane" : qUnion([Q0])});
            skPoint(sketch, "E52.0", {"position": v(-4.13, -204.74) * mm});
            skPoint(sketch, "E53.0", {"position": v(4.13, -209.74) * mm});
            skText(sketch, "E54", { "text": "24\n", "fontName": "OpenSans-Regular.ttf"});
            const initialGuessF21  = {"E54": [-0.00413, -0.20974, 1, 0, 0.005]};
            skSetInitialGuess(sketch, initialGuessF21);
            skSolve(sketch);
        }
        {
            var Q0;
            Q0 = qSketchRegion(id + "F21", true);
            extrude(context, id + "F22", {"entities" : qUnion([Q0]), "operationType" : NewBodyOperationType.REMOVE, "oppositeDirection" : true, "depth" : 0.4 * mm, "offsetDistance" : 25 * mm});
        }
    });
